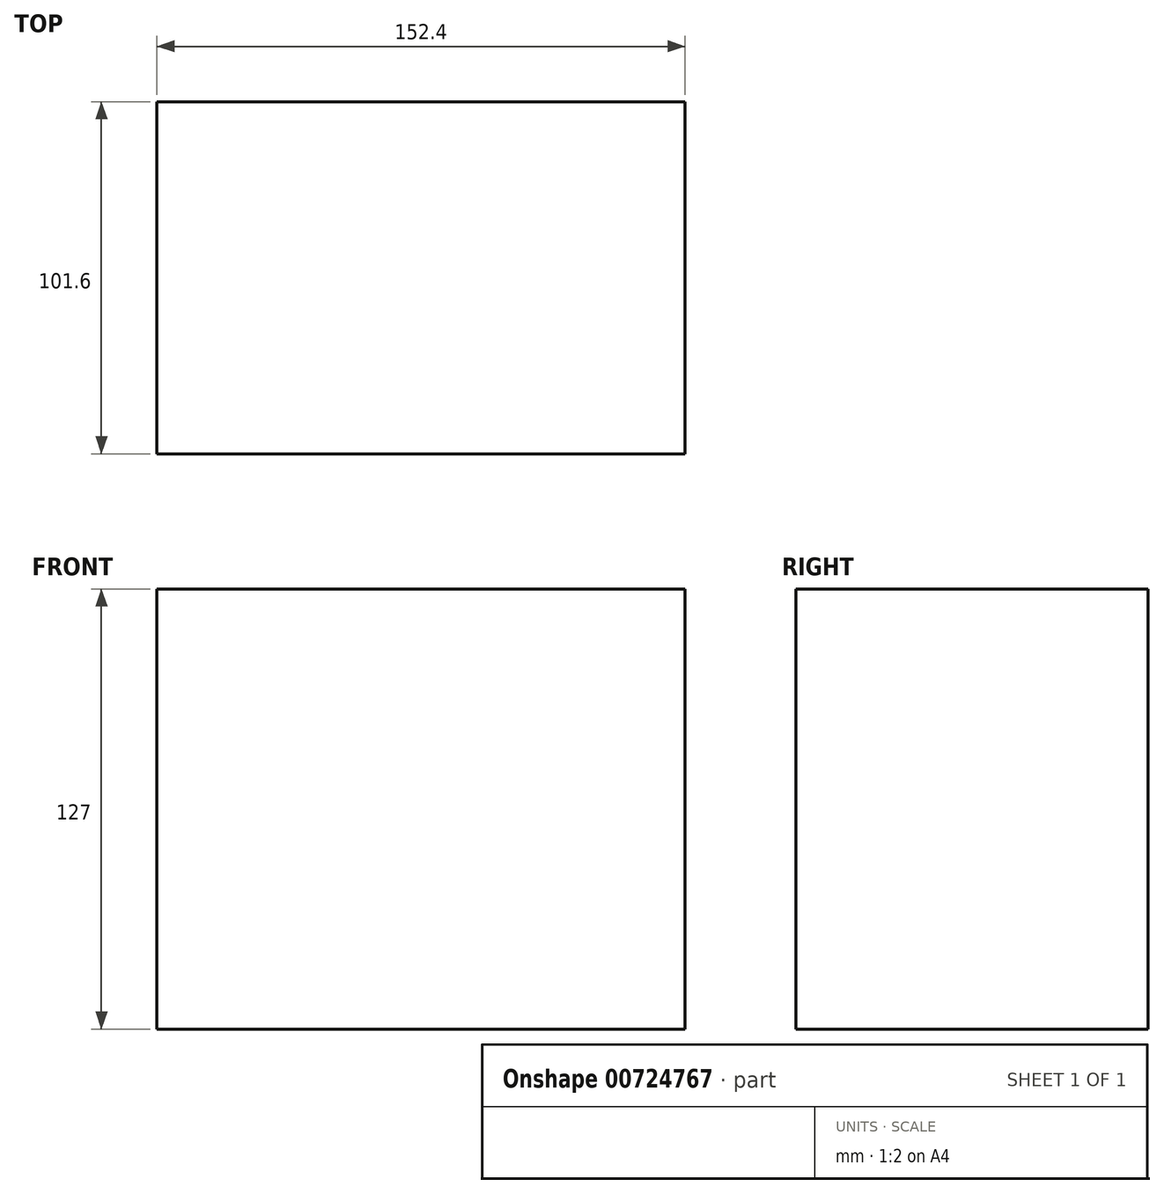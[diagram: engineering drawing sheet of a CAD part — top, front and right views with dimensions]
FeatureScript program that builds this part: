
annotation { "Feature Type Name" : "Feature", "Feature Type Description" : "" }
export const myFeature = defineFeature(function(context is Context, id is Id, definition is map)
    precondition{}
    {
        {
            var Q0;
            Q0=qCreatedBy(makeId("Front.planeOp"),FACE);
            var sketch = newSketch(context, id + "F0", { "sketchPlane" : qUnion([Q0])});
            skLineSegment(sketch, "E0", {"start": v(-76.23, -74.83) * mm, "end": v(76.17, -74.83) * mm});
            skLineSegment(sketch, "E1", {"start": v(76.17, -74.83) * mm, "end": v(76.17, 52.17) * mm});
            skLineSegment(sketch, "E2", {"start": v(76.17, 52.17) * mm, "end": v(-76.23, 52.17) * mm});
            skLineSegment(sketch, "E3", {"start": v(-76.23, 52.17) * mm, "end": v(-76.23, -74.83) * mm});
            skSolve(sketch);
        }
        {
            var Q0;
            Q0 = qSketchRegion(id + "F0", true);
            extrude(context, id + "F1", {"entities" : qUnion([Q0]), "depth" : 101.6 * mm, "offsetDistance" : 25.4 * mm});
        }
    });
